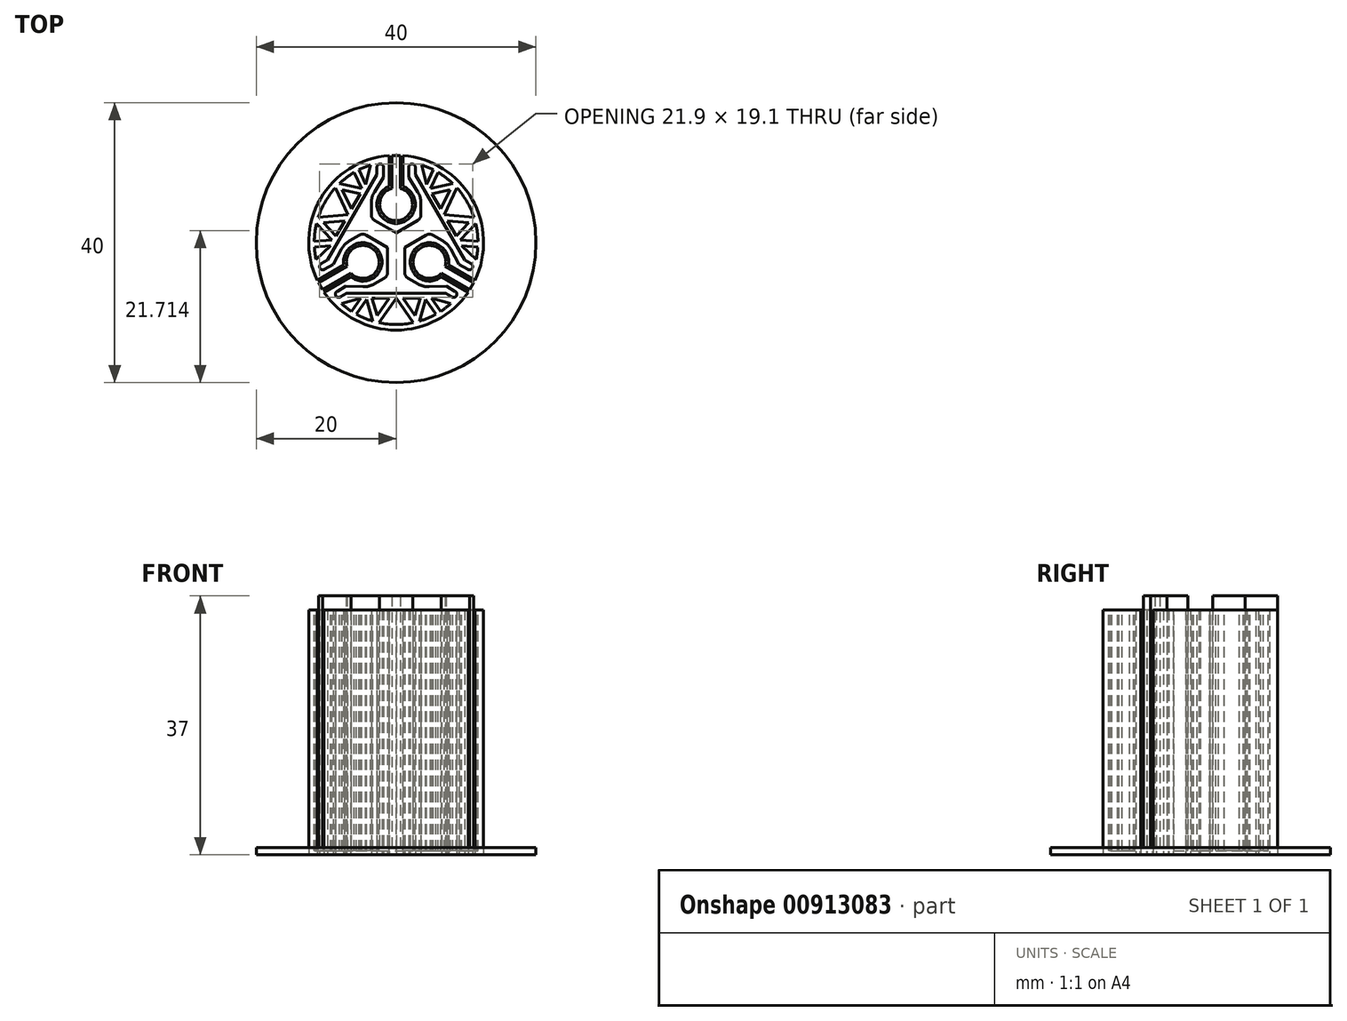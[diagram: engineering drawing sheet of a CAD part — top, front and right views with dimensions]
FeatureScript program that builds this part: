
annotation { "Feature Type Name" : "Feature", "Feature Type Description" : "" }
export const myFeature = defineFeature(function(context is Context, id is Id, definition is map)
    precondition{}
    {
        {
            var Q0;
            Q0=qCreatedBy(makeId("Top.planeOp"),FACE);
            var sketch = newSketch(context, id + "F0", { "sketchPlane" : qUnion([Q0])});
            skArc(sketch, "E0", {"start": v(-1, 8.06) * mm, "mid": v(0.5, 2.8) * mm, "end": v(0, 8.25) * mm});
            skLineSegment(sketch, "E1", {"start": v(-1, 8.06) * mm, "end": v(-1, 12.46) * mm});
            skLineSegment(sketch, "E2", {"start": v(0, 12.5) * mm, "end": v(0, 12.5) * mm});
            skLineSegment(sketch, "E3", {"start": v(0, 11.97) * mm, "end": v(0, 0) * mm, "construction": true});
            skArc(sketch, "E4", {"start": v(-1, 12.46) * mm, "mid": v(-10.83, 6.25) * mm, "end": v(-11.3, -5.36) * mm});
            skCircle(sketch, "E5", {"center": v(0, 0) * mm, "radius": 9.5 * mm, "construction": true});
            skLineSegment(sketch, "E6", {"start": v(0, 1.4) * mm, "end": v(-3.05, 3.16) * mm});
            skLineSegment(sketch, "E7", {"start": v(-3.55, 4.03) * mm, "end": v(-3.55, 5.66) * mm});
            skLineSegment(sketch, "E8", {"start": v(-3.1, 7.24) * mm, "end": v(-1.8, 9.33) * mm});
            skLineSegment(sketch, "E9", {"start": v(-1.8, 9.33) * mm, "end": v(-1.8, 10.79) * mm});
            skLineSegment(sketch, "E10", {"start": v(-2.75, 10.79) * mm, "end": v(-2.75, 9.74) * mm});
            skArc(sketch, "E11", {"start": v(-1.8, 10.79) * mm, "mid": v(-2.27, 11.26) * mm, "end": v(-2.75, 10.79) * mm});
            skLineSegment(sketch, "E12", {"start": v(-2.75, 9.74) * mm, "end": v(-9.35, -1.7) * mm});
            skPoint(sketch, "E13.visualSharp", {"position": v(-3.55, 6.51) * mm});
            skArc(sketch, "E13.filletArc", {"start": v(-3.1, 7.24) * mm, "mid": v(-3.43, 6.48) * mm, "end": v(-3.55, 5.66) * mm});
            skPoint(sketch, "E14.visualSharp", {"position": v(-3.55, 3.45) * mm});
            skArc(sketch, "E14.filletArc", {"start": v(-3.55, 4.03) * mm, "mid": v(-3.42, 3.53) * mm, "end": v(-3.05, 3.16) * mm});
            skLineSegment(sketch, "E15.MirrorCS", {"start": v(0, 1.4) * mm, "end": v(3.05, 3.16) * mm});
            skArc(sketch, "E16.MirrorCS", {"start": v(3.55, 4.03) * mm, "mid": v(3.42, 3.53) * mm, "end": v(3.05, 3.16) * mm});
            skLineSegment(sketch, "E17.MirrorCS", {"start": v(3.55, 4.03) * mm, "end": v(3.55, 5.66) * mm});
            skArc(sketch, "E18.MirrorCS", {"start": v(3.1, 7.24) * mm, "mid": v(3.43, 6.48) * mm, "end": v(3.55, 5.66) * mm});
            skLineSegment(sketch, "E19.MirrorCS", {"start": v(3.1, 7.24) * mm, "end": v(1.8, 9.33) * mm});
            skLineSegment(sketch, "E20.MirrorCS", {"start": v(1, 8.06) * mm, "end": v(1, 12.46) * mm});
            skLineSegment(sketch, "E21.MirrorCS", {"start": v(1.8, 9.33) * mm, "end": v(1.8, 10.79) * mm});
            skArc(sketch, "E22.MirrorCS", {"start": v(1.8, 10.79) * mm, "mid": v(2.27, 11.26) * mm, "end": v(2.75, 10.79) * mm});
            skLineSegment(sketch, "E23.MirrorCS", {"start": v(2.75, 10.79) * mm, "end": v(2.75, 9.74) * mm});
            skLineSegment(sketch, "E24.MirrorCS", {"start": v(2.75, 9.74) * mm, "end": v(9.35, -1.7) * mm});
            skArc(sketch, "E25.1.0", {"start": v(-6.48, -4.9) * mm, "mid": v(-2.68, -0.96) * mm, "end": v(-7.14, -4.12) * mm});
            skLineSegment(sketch, "E25.1.1", {"start": v(-1.21, -0.7) * mm, "end": v(-1.21, -4.22) * mm});
            skLineSegment(sketch, "E25.1.2", {"start": v(-1.21, -0.7) * mm, "end": v(-4.26, 1.06) * mm});
            skArc(sketch, "E25.1.3", {"start": v(-1.71, -5.09) * mm, "mid": v(-1.35, -4.72) * mm, "end": v(-1.21, -4.22) * mm});
            skArc(sketch, "E25.1.4", {"start": v(-5.26, 1.06) * mm, "mid": v(-4.76, 1.2) * mm, "end": v(-4.26, 1.06) * mm});
            skLineSegment(sketch, "E25.1.5", {"start": v(-1.71, -5.09) * mm, "end": v(-3.12, -5.9) * mm});
            skLineSegment(sketch, "E25.1.6", {"start": v(-5.26, 1.06) * mm, "end": v(-6.67, 0.25) * mm});
            skArc(sketch, "E25.1.7", {"start": v(-7.82, -0.94) * mm, "mid": v(-7.33, -0.27) * mm, "end": v(-6.67, 0.25) * mm});
            skLineSegment(sketch, "E25.1.8", {"start": v(-7.82, -0.94) * mm, "end": v(-8.98, -3.1) * mm});
            skArc(sketch, "E25.1.9", {"start": v(-4.72, -6.3) * mm, "mid": v(-3.9, -6.21) * mm, "end": v(-3.12, -5.9) * mm});
            skLineSegment(sketch, "E25.1.10", {"start": v(-4.72, -6.3) * mm, "end": v(-7.18, -6.22) * mm});
            skLineSegment(sketch, "E25.1.11", {"start": v(-7.18, -6.22) * mm, "end": v(-8.44, -6.95) * mm});
            skLineSegment(sketch, "E25.1.12", {"start": v(-8.98, -3.1) * mm, "end": v(-10.24, -3.84) * mm});
            skArc(sketch, "E25.1.13", {"start": v(-10.24, -3.84) * mm, "mid": v(-10.9, -3.66) * mm, "end": v(-10.72, -3.01) * mm});
            skArc(sketch, "E25.1.14", {"start": v(-8.44, -6.95) * mm, "mid": v(-8.62, -7.6) * mm, "end": v(-7.97, -7.78) * mm});
            skLineSegment(sketch, "E25.1.15", {"start": v(-7.97, -7.78) * mm, "end": v(-7.06, -7.25) * mm});
            skLineSegment(sketch, "E25.1.16", {"start": v(-10.72, -3.01) * mm, "end": v(-9.8, -2.49) * mm});
            skLineSegment(sketch, "E25.1.17", {"start": v(-9.8, -2.49) * mm, "end": v(-3.2, 8.94) * mm});
            skArc(sketch, "E25.2.0", {"start": v(7.48, -3.16) * mm, "mid": v(2.17, -1.84) * mm, "end": v(7.14, -4.12) * mm});
            skLineSegment(sketch, "E25.2.1", {"start": v(1.21, -0.7) * mm, "end": v(4.26, 1.06) * mm});
            skLineSegment(sketch, "E25.2.2", {"start": v(1.21, -0.7) * mm, "end": v(1.21, -4.22) * mm});
            skArc(sketch, "E25.2.3", {"start": v(5.26, 1.06) * mm, "mid": v(4.76, 1.2) * mm, "end": v(4.26, 1.06) * mm});
            skArc(sketch, "E25.2.4", {"start": v(1.71, -5.09) * mm, "mid": v(1.35, -4.72) * mm, "end": v(1.21, -4.22) * mm});
            skLineSegment(sketch, "E25.2.5", {"start": v(5.26, 1.06) * mm, "end": v(6.67, 0.25) * mm});
            skLineSegment(sketch, "E25.2.6", {"start": v(1.71, -5.09) * mm, "end": v(3.12, -5.9) * mm});
            skArc(sketch, "E25.2.7", {"start": v(4.72, -6.3) * mm, "mid": v(3.9, -6.21) * mm, "end": v(3.12, -5.9) * mm});
            skLineSegment(sketch, "E25.2.8", {"start": v(4.72, -6.3) * mm, "end": v(7.18, -6.22) * mm});
            skArc(sketch, "E25.2.9", {"start": v(7.82, -0.94) * mm, "mid": v(7.33, -0.27) * mm, "end": v(6.67, 0.25) * mm});
            skLineSegment(sketch, "E25.2.10", {"start": v(7.82, -0.94) * mm, "end": v(8.98, -3.1) * mm});
            skLineSegment(sketch, "E25.2.11", {"start": v(8.98, -3.1) * mm, "end": v(10.24, -3.84) * mm});
            skLineSegment(sketch, "E25.2.12", {"start": v(7.18, -6.22) * mm, "end": v(8.44, -6.95) * mm});
            skArc(sketch, "E25.2.13", {"start": v(8.44, -6.95) * mm, "mid": v(8.62, -7.6) * mm, "end": v(7.97, -7.78) * mm});
            skArc(sketch, "E25.2.14", {"start": v(10.24, -3.84) * mm, "mid": v(10.9, -3.66) * mm, "end": v(10.72, -3.01) * mm});
            skLineSegment(sketch, "E25.2.15", {"start": v(10.72, -3.01) * mm, "end": v(9.8, -2.49) * mm});
            skLineSegment(sketch, "E25.2.16", {"start": v(7.97, -7.78) * mm, "end": v(7.06, -7.25) * mm});
            skLineSegment(sketch, "E25.2.17", {"start": v(7.06, -7.25) * mm, "end": v(-6.14, -7.25) * mm});
            skLineSegment(sketch, "E26.1.0", {"start": v(-6.48, -4.9) * mm, "end": v(-10.3, -7.1) * mm});
            skLineSegment(sketch, "E26.1.1", {"start": v(-7.48, -3.16) * mm, "end": v(-11.3, -5.36) * mm});
            skLineSegment(sketch, "E26.2.0", {"start": v(7.48, -3.16) * mm, "end": v(11.3, -5.36) * mm});
            skLineSegment(sketch, "E26.2.1", {"start": v(6.48, -4.9) * mm, "end": v(10.3, -7.1) * mm});
            skArc(sketch, "E27.trimOffspring", {"start": v(-10.3, -7.1) * mm, "mid": v(0, -12.5) * mm, "end": v(10.3, -7.1) * mm});
            skArc(sketch, "E28.trimOffspring", {"start": v(11.3, -5.36) * mm, "mid": v(10.57, 6.68) * mm, "end": v(0, 12.5) * mm});
            skLineSegment(sketch, "E29", {"start": v(-7.06, -7.25) * mm, "end": v(-6.14, -7.25) * mm});
            skLineSegment(sketch, "E30", {"start": v(9.35, -1.7) * mm, "end": v(9.8, -2.49) * mm});
            skSolve(sketch);
        }
        {
            var Q0;
            {var subQ3=sQuery(id+"F0.wireOp",EDGE,"E1");Q0=makeQuery(id+"F0.imprint","IMPRINT",FACE,{"disambiguationData":[TD([[makeQuery(id+"F0.imprint","IMPRINT",EDGE,{"derivedFrom":subQ3}),1.0]])]});}
            extrude(context, id + "F1", {"entities" : qUnion([Q0]), "depth" : 35 * mm, "offsetDistance" : 25 * mm});
        }
        {
            var Q0;
            Q0=makeQuery(id+"F1.opExtrude","CAP_FACE",FACE,{"disambiguationData":[OSD([sQuery(id+"F0.wireOp",EDGE,"E0"),sQuery(id+"F0.wireOp",EDGE,"E1"),sQuery(id+"F0.wireOp",EDGE,"E4"),sQuery(id+"F0.wireOp",EDGE,"E6"),sQuery(id+"F0.wireOp",EDGE,"E7"),sQuery(id+"F0.wireOp",EDGE,"E8"),sQuery(id+"F0.wireOp",EDGE,"E9"),sQuery(id+"F0.wireOp",EDGE,"E10"),sQuery(id+"F0.wireOp",EDGE,"E11"),sQuery(id+"F0.wireOp",EDGE,"E12"),sQuery(id+"F0.wireOp",EDGE,"E13.filletArc"),sQuery(id+"F0.wireOp",EDGE,"E14.filletArc"),sQuery(id+"F0.wireOp",EDGE,"E15.MirrorCS"),sQuery(id+"F0.wireOp",EDGE,"E16.MirrorCS"),sQuery(id+"F0.wireOp",EDGE,"E17.MirrorCS"),sQuery(id+"F0.wireOp",EDGE,"E18.MirrorCS"),sQuery(id+"F0.wireOp",EDGE,"E19.MirrorCS"),sQuery(id+"F0.wireOp",EDGE,"E20.MirrorCS"),sQuery(id+"F0.wireOp",EDGE,"E21.MirrorCS"),sQuery(id+"F0.wireOp",EDGE,"E22.MirrorCS"),sQuery(id+"F0.wireOp",EDGE,"E23.MirrorCS"),sQuery(id+"F0.wireOp",EDGE,"E24.MirrorCS"),sQuery(id+"F0.wireOp",EDGE,"E25.1.0"),sQuery(id+"F0.wireOp",EDGE,"E25.1.1"),sQuery(id+"F0.wireOp",EDGE,"E25.1.2"),sQuery(id+"F0.wireOp",EDGE,"E25.1.3"),sQuery(id+"F0.wireOp",EDGE,"E25.1.4"),sQuery(id+"F0.wireOp",EDGE,"E25.1.5"),sQuery(id+"F0.wireOp",EDGE,"E25.1.6"),sQuery(id+"F0.wireOp",EDGE,"E25.1.7"),sQuery(id+"F0.wireOp",EDGE,"E25.1.8"),sQuery(id+"F0.wireOp",EDGE,"E25.1.9"),sQuery(id+"F0.wireOp",EDGE,"E25.1.10"),sQuery(id+"F0.wireOp",EDGE,"E25.1.11"),sQuery(id+"F0.wireOp",EDGE,"E25.1.12"),sQuery(id+"F0.wireOp",EDGE,"E25.1.13"),sQuery(id+"F0.wireOp",EDGE,"E25.1.14"),sQuery(id+"F0.wireOp",EDGE,"E25.1.15"),sQuery(id+"F0.wireOp",EDGE,"E25.1.16"),sQuery(id+"F0.wireOp",EDGE,"E25.1.17"),sQuery(id+"F0.wireOp",EDGE,"E25.2.0"),sQuery(id+"F0.wireOp",EDGE,"E25.2.1"),sQuery(id+"F0.wireOp",EDGE,"E25.2.2"),sQuery(id+"F0.wireOp",EDGE,"E25.2.3"),sQuery(id+"F0.wireOp",EDGE,"E25.2.4"),sQuery(id+"F0.wireOp",EDGE,"E25.2.5"),sQuery(id+"F0.wireOp",EDGE,"E25.2.6"),sQuery(id+"F0.wireOp",EDGE,"E25.2.7"),sQuery(id+"F0.wireOp",EDGE,"E25.2.8"),sQuery(id+"F0.wireOp",EDGE,"E25.2.9"),sQuery(id+"F0.wireOp",EDGE,"E25.2.10"),sQuery(id+"F0.wireOp",EDGE,"E25.2.11"),sQuery(id+"F0.wireOp",EDGE,"E25.2.12"),sQuery(id+"F0.wireOp",EDGE,"E25.2.13"),sQuery(id+"F0.wireOp",EDGE,"E25.2.14"),sQuery(id+"F0.wireOp",EDGE,"E25.2.15"),sQuery(id+"F0.wireOp",EDGE,"E25.2.16"),sQuery(id+"F0.wireOp",EDGE,"E25.2.17"),sQuery(id+"F0.wireOp",EDGE,"E26.1.0"),sQuery(id+"F0.wireOp",EDGE,"E26.1.1"),sQuery(id+"F0.wireOp",EDGE,"E26.2.0"),sQuery(id+"F0.wireOp",EDGE,"E26.2.1"),sQuery(id+"F0.wireOp",EDGE,"E27.trimOffspring"),sQuery(id+"F0.wireOp",EDGE,"E28.trimOffspring"),sQuery(id+"F0.wireOp",EDGE,"E29"),sQuery(id+"F0.wireOp",EDGE,"E30")])],"isStart":false});
            var sketch = newSketch(context, id + "F2", { "sketchPlane" : qUnion([Q0])});
            skArc(sketch, "E31.0", {"start": v(-9.63, -6.64) * mm, "mid": v(0, -11.7) * mm, "end": v(9.63, -6.64) * mm});
            skLineSegment(sketch, "E32", {"start": v(-3.34, -12.05) * mm, "end": v(0, -7.25) * mm});
            skLineSegment(sketch, "E33", {"start": v(-2.85, -11.35) * mm, "end": v(-4.1, -7.25) * mm});
            skLineSegment(sketch, "E34", {"start": v(-4.1, -7.25) * mm, "end": v(-6.48, -10.69) * mm});
            skArc(sketch, "E35.0.startCap", {"start": v(-3.7, -7.13) * mm, "mid": v(-3.7, -7.31) * mm, "end": v(-3.76, -7.48) * mm});
            skLineSegment(sketch, "E35.0.left", {"start": v(-3.76, -7.48) * mm, "end": v(-6.15, -10.92) * mm});
            skLineSegment(sketch, "E35.0.right", {"start": v(-4.42, -7.02) * mm, "end": v(-6.81, -10.46) * mm});
            skArc(sketch, "E35.1.startCap", {"start": v(-2.47, -11.23) * mm, "mid": v(-2.73, -11.73) * mm, "end": v(-3.23, -11.46) * mm});
            skArc(sketch, "E35.1.endCap", {"start": v(-4.47, -7.37) * mm, "mid": v(-4.49, -7.19) * mm, "end": v(-4.42, -7.02) * mm});
            skLineSegment(sketch, "E35.1.left", {"start": v(-3.23, -11.46) * mm, "end": v(-4.47, -7.37) * mm});
            skLineSegment(sketch, "E35.1.right", {"start": v(-2.47, -11.23) * mm, "end": v(-3.7, -7.13) * mm});
            skLineSegment(sketch, "E35.2.left", {"start": v(-3.66, -11.82) * mm, "end": v(-0.33, -7.02) * mm});
            skLineSegment(sketch, "E35.2.right", {"start": v(-3, -12.28) * mm, "end": v(0.33, -7.48) * mm});
            skLineSegment(sketch, "E36", {"start": v(-7.8, -8.72) * mm, "end": v(-5.05, -7.93) * mm});
            skLineSegment(sketch, "E37", {"start": v(-5.05, -7.93) * mm, "end": v(-0.96, -7.93) * mm});
            skLineSegment(sketch, "E38.MirrorCS", {"start": v(3, -12.28) * mm, "end": v(-0.33, -7.48) * mm});
            skLineSegment(sketch, "E39.MirrorCS", {"start": v(3.66, -11.82) * mm, "end": v(0.33, -7.02) * mm});
            skLineSegment(sketch, "E40.MirrorCS", {"start": v(2.47, -11.23) * mm, "end": v(3.7, -7.13) * mm});
            skLineSegment(sketch, "E41.MirrorCS", {"start": v(5.05, -7.93) * mm, "end": v(0.96, -7.93) * mm});
            skLineSegment(sketch, "E42.MirrorCS", {"start": v(3.76, -7.48) * mm, "end": v(6.15, -10.92) * mm});
            skLineSegment(sketch, "E43.MirrorCS", {"start": v(3.23, -11.46) * mm, "end": v(4.47, -7.37) * mm});
            skLineSegment(sketch, "E44.MirrorCS", {"start": v(4.42, -7.02) * mm, "end": v(6.81, -10.46) * mm});
            skLineSegment(sketch, "E45.MirrorCS", {"start": v(7.8, -8.72) * mm, "end": v(5.05, -7.93) * mm});
            skLineSegment(sketch, "E46.1.0", {"start": v(11.45, -2.39) * mm, "end": v(9.4, -0.41) * mm});
            skLineSegment(sketch, "E46.1.1", {"start": v(8.3, -0.32) * mm, "end": v(12.46, -0.67) * mm});
            skLineSegment(sketch, "E46.1.2", {"start": v(8.36, 0.48) * mm, "end": v(12.53, 0.13) * mm});
            skLineSegment(sketch, "E46.1.3", {"start": v(11.54, 2.93) * mm, "end": v(8.62, -0.2) * mm});
            skLineSegment(sketch, "E46.1.4", {"start": v(10.96, 3.48) * mm, "end": v(8.03, 0.35) * mm});
            skLineSegment(sketch, "E46.1.5", {"start": v(9.4, -0.41) * mm, "end": v(7.35, 3.13) * mm});
            skLineSegment(sketch, "E46.1.6", {"start": v(12.07, 2.74) * mm, "end": v(6.24, 3.23) * mm});
            skLineSegment(sketch, "E46.1.7", {"start": v(12.13, 3.53) * mm, "end": v(6.31, 4.02) * mm});
            skLineSegment(sketch, "E46.1.8", {"start": v(9.13, 8.74) * mm, "end": v(6.64, 3.45) * mm});
            skLineSegment(sketch, "E46.1.9", {"start": v(8.4, 9.08) * mm, "end": v(5.92, 3.8) * mm});
            skLineSegment(sketch, "E46.1.10", {"start": v(4.34, 8.34) * mm, "end": v(6.39, 4.8) * mm});
            skLineSegment(sketch, "E46.1.11", {"start": v(8.5, 7.75) * mm, "end": v(4.32, 6.78) * mm});
            skLineSegment(sketch, "E46.1.12", {"start": v(8.31, 8.53) * mm, "end": v(4.14, 7.56) * mm});
            skLineSegment(sketch, "E46.1.13", {"start": v(4.6, 7) * mm, "end": v(6.38, 10.79) * mm});
            skLineSegment(sketch, "E46.1.14", {"start": v(3.87, 7.34) * mm, "end": v(5.65, 11.13) * mm});
            skLineSegment(sketch, "E46.1.15", {"start": v(3.66, 11.11) * mm, "end": v(4.34, 8.34) * mm});
            skArc(sketch, "E46.1.16", {"start": v(10.57, -5.02) * mm, "mid": v(10.13, 5.85) * mm, "end": v(0.94, 11.66) * mm});
            skLineSegment(sketch, "E46.2.0", {"start": v(-3.66, 11.11) * mm, "end": v(-4.34, 8.34) * mm});
            skLineSegment(sketch, "E46.2.1", {"start": v(-3.87, 7.34) * mm, "end": v(-5.65, 11.13) * mm});
            skLineSegment(sketch, "E46.2.2", {"start": v(-4.6, 7) * mm, "end": v(-6.38, 10.79) * mm});
            skLineSegment(sketch, "E46.2.3", {"start": v(-8.31, 8.53) * mm, "end": v(-4.14, 7.56) * mm});
            skLineSegment(sketch, "E46.2.4", {"start": v(-8.5, 7.75) * mm, "end": v(-4.32, 6.78) * mm});
            skLineSegment(sketch, "E46.2.5", {"start": v(-4.34, 8.34) * mm, "end": v(-6.39, 4.8) * mm});
            skLineSegment(sketch, "E46.2.6", {"start": v(-8.4, 9.08) * mm, "end": v(-5.92, 3.8) * mm});
            skLineSegment(sketch, "E46.2.7", {"start": v(-9.13, 8.74) * mm, "end": v(-6.64, 3.45) * mm});
            skLineSegment(sketch, "E46.2.8", {"start": v(-12.13, 3.53) * mm, "end": v(-6.31, 4.02) * mm});
            skLineSegment(sketch, "E46.2.9", {"start": v(-12.07, 2.74) * mm, "end": v(-6.24, 3.23) * mm});
            skLineSegment(sketch, "E46.2.10", {"start": v(-9.4, -0.41) * mm, "end": v(-7.35, 3.13) * mm});
            skLineSegment(sketch, "E46.2.11", {"start": v(-10.96, 3.48) * mm, "end": v(-8.03, 0.35) * mm});
            skLineSegment(sketch, "E46.2.12", {"start": v(-11.54, 2.93) * mm, "end": v(-8.62, -0.2) * mm});
            skLineSegment(sketch, "E46.2.13", {"start": v(-8.36, 0.48) * mm, "end": v(-12.53, 0.13) * mm});
            skLineSegment(sketch, "E46.2.14", {"start": v(-8.3, -0.32) * mm, "end": v(-12.46, -0.67) * mm});
            skLineSegment(sketch, "E46.2.15", {"start": v(-11.45, -2.39) * mm, "end": v(-9.4, -0.41) * mm});
            skArc(sketch, "E46.2.16", {"start": v(-0.94, 11.66) * mm, "mid": v(-10.13, 5.85) * mm, "end": v(-10.57, -5.02) * mm});
            skSolve(sketch);
        }
        {
            var Q0;
            {var subQ0=sQuery(id+"F2.wireOp",EDGE,"E36");Q0=makeQuery(id+"F2.imprint","IMPRINT",FACE,{"disambiguationData":[TD([[makeQuery(id+"F2.imprint","IMPRINT",EDGE,{"derivedFrom":subQ0}),-1.0]])]});}
            var Q1;
            {var subQ0=sQuery(id+"F2.wireOp",EDGE,"E35.0.left");var subQ1=sQuery(id+"F2.wireOp",EDGE,"E31.0");var subQ2=makeQuery(id+"F2.imprint","INTERSECT",VERTEX,{"derivedFrom":[subQ1,subQ0]});Q1=makeQuery(id+"F2.imprint","IMPRINT",FACE,{"disambiguationData":[TD([[makeQuery(id+"F2.imprint","IMPRINT",EDGE,{"disambiguationData":[TD([[subQ2,-1.0]])],"derivedFrom":subQ1}),1.0]])]});}
            var Q2;
            {var subQ0=sQuery(id+"F2.wireOp",EDGE,"E35.2.left");var subQ1=sQuery(id+"F2.wireOp",EDGE,"E35.1.right");var subQ2=makeQuery(id+"F2.imprint","INTERSECT",VERTEX,{"derivedFrom":[subQ1,subQ0]});Q2=makeQuery(id+"F2.imprint","IMPRINT",FACE,{"disambiguationData":[TD([[makeQuery(id+"F2.imprint","IMPRINT",EDGE,{"disambiguationData":[TD([[subQ2,-1.0]])],"derivedFrom":subQ1}),-1.0]])]});}
            var Q3;
            {var subQ0=sQuery(id+"F2.wireOp",EDGE,"E35.2.right");var subQ1=sQuery(id+"F2.wireOp",EDGE,"E31.0");var subQ2=makeQuery(id+"F2.imprint","INTERSECT",VERTEX,{"derivedFrom":[subQ1,subQ0]});Q3=makeQuery(id+"F2.imprint","IMPRINT",FACE,{"disambiguationData":[TD([[makeQuery(id+"F2.imprint","IMPRINT",EDGE,{"disambiguationData":[TD([[subQ2,-1.0]])],"derivedFrom":subQ1}),1.0]])]});}
            var Q4;
            {var subQ0=sQuery(id+"F2.wireOp",EDGE,"E41.MirrorCS");var subQ1=sQuery(id+"F2.wireOp",EDGE,"E39.MirrorCS");var subQ2=makeQuery(id+"F2.imprint","INTERSECT",VERTEX,{"derivedFrom":[subQ1,subQ0]});Q4=makeQuery(id+"F2.imprint","IMPRINT",FACE,{"disambiguationData":[TD([[makeQuery(id+"F2.imprint","IMPRINT",EDGE,{"disambiguationData":[TD([[subQ2,1.0]])],"derivedFrom":subQ1}),-1.0]])]});}
            var Q5;
            {var subQ0=sQuery(id+"F2.wireOp",EDGE,"E43.MirrorCS");var subQ1=sQuery(id+"F2.wireOp",EDGE,"E31.0");var subQ2=makeQuery(id+"F2.imprint","INTERSECT",VERTEX,{"derivedFrom":[subQ1,subQ0]});Q5=makeQuery(id+"F2.imprint","IMPRINT",FACE,{"disambiguationData":[TD([[makeQuery(id+"F2.imprint","IMPRINT",EDGE,{"disambiguationData":[TD([[subQ2,-1.0]])],"derivedFrom":subQ1}),1.0]])]});}
            var Q6;
            {var subQ0=sQuery(id+"F2.wireOp",EDGE,"E45.MirrorCS");Q6=makeQuery(id+"F2.imprint","IMPRINT",FACE,{"disambiguationData":[TD([[makeQuery(id+"F2.imprint","IMPRINT",EDGE,{"derivedFrom":subQ0}),1.0]])]});}
            var Q7;
            {var subQ0=sQuery(id+"F2.wireOp",EDGE,"E46.1.0");Q7=makeQuery(id+"F2.imprint","IMPRINT",FACE,{"disambiguationData":[TD([[makeQuery(id+"F2.imprint","IMPRINT",EDGE,{"derivedFrom":subQ0}),-1.0]])]});}
            var Q8;
            {var subQ0=sQuery(id+"F2.wireOp",EDGE,"E46.1.3");var subQ1=sQuery(id+"F2.wireOp",EDGE,"E46.1.2");var subQ2=makeQuery(id+"F2.imprint","INTERSECT",VERTEX,{"derivedFrom":[subQ1,subQ0]});Q8=makeQuery(id+"F2.imprint","IMPRINT",FACE,{"disambiguationData":[TD([[makeQuery(id+"F2.imprint","IMPRINT",EDGE,{"disambiguationData":[TD([[subQ2,-1.0]])],"derivedFrom":subQ1}),1.0]])]});}
            var Q9;
            {var subQ0=sQuery(id+"F2.wireOp",EDGE,"E46.1.6");var subQ1=sQuery(id+"F2.wireOp",EDGE,"E46.1.4");var subQ2=makeQuery(id+"F2.imprint","INTERSECT",VERTEX,{"derivedFrom":[subQ1,subQ0]});Q9=makeQuery(id+"F2.imprint","IMPRINT",FACE,{"disambiguationData":[TD([[makeQuery(id+"F2.imprint","IMPRINT",EDGE,{"disambiguationData":[TD([[subQ2,-1.0]])],"derivedFrom":subQ1}),-1.0]])]});}
            var Q10;
            {var subQ0=sQuery(id+"F2.wireOp",EDGE,"E46.2.10");var subQ1=sQuery(id+"F2.wireOp",EDGE,"E46.2.9");var subQ2=makeQuery(id+"F2.imprint","INTERSECT",VERTEX,{"derivedFrom":[subQ1,subQ0]});Q10=makeQuery(id+"F2.imprint","IMPRINT",FACE,{"disambiguationData":[TD([[makeQuery(id+"F2.imprint","IMPRINT",EDGE,{"disambiguationData":[TD([[subQ2,1.0]])],"derivedFrom":subQ1}),-1.0]])]});}
            var Q11;
            {var subQ0=sQuery(id+"F2.wireOp",EDGE,"E46.2.16");var subQ1=sQuery(id+"F2.wireOp",EDGE,"E46.2.12");var subQ2=makeQuery(id+"F2.imprint","INTERSECT",VERTEX,{"derivedFrom":[subQ1,subQ0]});Q11=makeQuery(id+"F2.imprint","IMPRINT",FACE,{"disambiguationData":[TD([[makeQuery(id+"F2.imprint","IMPRINT",EDGE,{"disambiguationData":[TD([[subQ2,-1.0]])],"derivedFrom":subQ1}),-1.0]])]});}
            var Q12;
            {var subQ0=sQuery(id+"F2.wireOp",EDGE,"E46.2.15");Q12=makeQuery(id+"F2.imprint","IMPRINT",FACE,{"disambiguationData":[TD([[makeQuery(id+"F2.imprint","IMPRINT",EDGE,{"derivedFrom":subQ0}),1.0]])]});}
            var Q13;
            {var subQ0=sQuery(id+"F2.wireOp",EDGE,"E46.2.8");var subQ1=sQuery(id+"F2.wireOp",EDGE,"E46.2.7");var subQ2=makeQuery(id+"F2.imprint","INTERSECT",VERTEX,{"derivedFrom":[subQ1,subQ0]});Q13=makeQuery(id+"F2.imprint","IMPRINT",FACE,{"disambiguationData":[TD([[makeQuery(id+"F2.imprint","IMPRINT",EDGE,{"disambiguationData":[TD([[subQ2,1.0]])],"derivedFrom":subQ1}),-1.0]])]});}
            var Q14;
            {var subQ0=sQuery(id+"F2.wireOp",EDGE,"E46.2.6");var subQ1=sQuery(id+"F2.wireOp",EDGE,"E46.2.4");var subQ2=makeQuery(id+"F2.imprint","INTERSECT",VERTEX,{"derivedFrom":[subQ1,subQ0]});Q14=makeQuery(id+"F2.imprint","IMPRINT",FACE,{"disambiguationData":[TD([[makeQuery(id+"F2.imprint","IMPRINT",EDGE,{"disambiguationData":[TD([[subQ2,-1.0]])],"derivedFrom":subQ1}),-1.0]])]});}
            var Q15;
            {var subQ0=sQuery(id+"F2.wireOp",EDGE,"E46.2.3");var subQ1=sQuery(id+"F2.wireOp",EDGE,"E46.2.2");var subQ2=makeQuery(id+"F2.imprint","INTERSECT",VERTEX,{"derivedFrom":[subQ1,subQ0]});Q15=makeQuery(id+"F2.imprint","IMPRINT",FACE,{"disambiguationData":[TD([[makeQuery(id+"F2.imprint","IMPRINT",EDGE,{"disambiguationData":[TD([[subQ2,-1.0]])],"derivedFrom":subQ1}),1.0]])]});}
            var Q16;
            {var subQ0=sQuery(id+"F2.wireOp",EDGE,"E46.2.0");Q16=makeQuery(id+"F2.imprint","IMPRINT",FACE,{"disambiguationData":[TD([[makeQuery(id+"F2.imprint","IMPRINT",EDGE,{"derivedFrom":subQ0}),-1.0]])]});}
            var Q17;
            {var subQ0=sQuery(id+"F2.wireOp",EDGE,"E46.1.15");Q17=makeQuery(id+"F2.imprint","IMPRINT",FACE,{"disambiguationData":[TD([[makeQuery(id+"F2.imprint","IMPRINT",EDGE,{"derivedFrom":subQ0}),1.0]])]});}
            var Q18;
            {var subQ0=sQuery(id+"F2.wireOp",EDGE,"E46.1.16");var subQ1=sQuery(id+"F2.wireOp",EDGE,"E46.1.12");var subQ2=makeQuery(id+"F2.imprint","INTERSECT",VERTEX,{"derivedFrom":[subQ1,subQ0]});Q18=makeQuery(id+"F2.imprint","IMPRINT",FACE,{"disambiguationData":[TD([[makeQuery(id+"F2.imprint","IMPRINT",EDGE,{"disambiguationData":[TD([[subQ2,-1.0]])],"derivedFrom":subQ1}),-1.0]])]});}
            var Q19;
            {var subQ0=sQuery(id+"F2.wireOp",EDGE,"E46.1.10");var subQ1=sQuery(id+"F2.wireOp",EDGE,"E46.1.9");var subQ2=makeQuery(id+"F2.imprint","INTERSECT",VERTEX,{"derivedFrom":[subQ1,subQ0]});Q19=makeQuery(id+"F2.imprint","IMPRINT",FACE,{"disambiguationData":[TD([[makeQuery(id+"F2.imprint","IMPRINT",EDGE,{"disambiguationData":[TD([[subQ2,1.0]])],"derivedFrom":subQ1}),-1.0]])]});}
            var Q20;
            {var subQ0=sQuery(id+"F2.wireOp",EDGE,"E46.1.8");var subQ1=sQuery(id+"F2.wireOp",EDGE,"E46.1.7");var subQ2=makeQuery(id+"F2.imprint","INTERSECT",VERTEX,{"derivedFrom":[subQ1,subQ0]});Q20=makeQuery(id+"F2.imprint","IMPRINT",FACE,{"disambiguationData":[TD([[makeQuery(id+"F2.imprint","IMPRINT",EDGE,{"disambiguationData":[TD([[subQ2,1.0]])],"derivedFrom":subQ1}),-1.0]])]});}
            extrude(context, id + "F3", {"entities" : qUnion([Q0, Q1, Q2, Q3, Q4, Q5, Q6, Q7, Q8, Q9, Q10, Q11, Q12, Q13, Q14, Q15, Q16, Q17, Q18, Q19, Q20]), "operationType" : NewBodyOperationType.REMOVE, "oppositeDirection" : true, "depth" : 34.4 * mm, "offsetDistance" : 25 * mm});
        }
        {
            var Q0;
            Q0=qCreatedBy(makeId("Top.planeOp"),FACE);
            var sketch = newSketch(context, id + "F4", { "sketchPlane" : qUnion([Q0])});
            skCircle(sketch, "E47", {"center": v(0, 0) * mm, "radius": 20 * mm});
            skLineSegment(sketch, "E48.0", {"start": v(-7.03, -3.37) * mm, "end": v(-11.1, -5.71) * mm});
            skArc(sketch, "E49", {"start": v(-6.43, -4.4) * mm, "mid": v(-2.73, -1.57) * mm, "end": v(-7.03, -3.37) * mm});
            skLineSegment(sketch, "E50", {"start": v(-10.5, -6.75) * mm, "end": v(-6.43, -4.4) * mm});
            skLineSegment(sketch, "E51", {"start": v(-11.1, -5.71) * mm, "end": v(-10.5, -6.75) * mm});
            skLineSegment(sketch, "E52.1.0", {"start": v(6.43, -4.4) * mm, "end": v(10.5, -6.75) * mm});
            skLineSegment(sketch, "E52.1.1", {"start": v(10.5, -6.75) * mm, "end": v(11.1, -5.71) * mm});
            skLineSegment(sketch, "E52.1.2", {"start": v(11.1, -5.71) * mm, "end": v(7.03, -3.37) * mm});
            skArc(sketch, "E52.1.3", {"start": v(7.03, -3.37) * mm, "mid": v(2.73, -1.57) * mm, "end": v(6.43, -4.4) * mm});
            skLineSegment(sketch, "E52.2.0", {"start": v(0.6, 7.77) * mm, "end": v(0.6, 12.46) * mm});
            skLineSegment(sketch, "E52.2.1", {"start": v(0.6, 12.46) * mm, "end": v(-0.6, 12.46) * mm});
            skLineSegment(sketch, "E52.2.2", {"start": v(-0.6, 12.46) * mm, "end": v(-0.6, 7.77) * mm});
            skArc(sketch, "E52.2.3", {"start": v(-0.6, 7.77) * mm, "mid": v(0, 3.15) * mm, "end": v(0.6, 7.77) * mm});
            skSolve(sketch);
        }
        {
            var Q0;
            Q0=makeQuery(id+"F4.imprint","IMPRINT",FACE,{"disambiguationData":[TD([[makeQuery(id+"F4.imprint","IMPRINT",EDGE,{"derivedFrom":sQuery(id+"F4.wireOp",EDGE,"E47")}),1.0]])]});
            extrude(context, id + "F5", {"entities" : qUnion([Q0]), "depth" : 1 * mm, "offsetDistance" : 25 * mm});
        }
        {
            var Q0;
            Q0=makeQuery(id+"F4.imprint","IMPRINT",FACE,{"disambiguationData":[TD([[makeQuery(id+"F4.imprint","IMPRINT",EDGE,{"derivedFrom":sQuery(id+"F4.wireOp",EDGE,"E48.0")}),1.0]])]});
            var Q1;
            Q1=makeQuery(id+"F4.imprint","IMPRINT",FACE,{"disambiguationData":[TD([[makeQuery(id+"F4.imprint","IMPRINT",EDGE,{"derivedFrom":sQuery(id+"F4.wireOp",EDGE,"E52.1.0")}),1.0]])]});
            var Q2;
            Q2=makeQuery(id+"F4.imprint","IMPRINT",FACE,{"disambiguationData":[TD([[makeQuery(id+"F4.imprint","IMPRINT",EDGE,{"derivedFrom":sQuery(id+"F4.wireOp",EDGE,"E52.2.0")}),1.0]])]});
            extrude(context, id + "F6", {"entities" : qUnion([Q0, Q1, Q2]), "operationType" : NewBodyOperationType.ADD, "depth" : 37 * mm, "offsetDistance" : 25 * mm});
        }
    });
